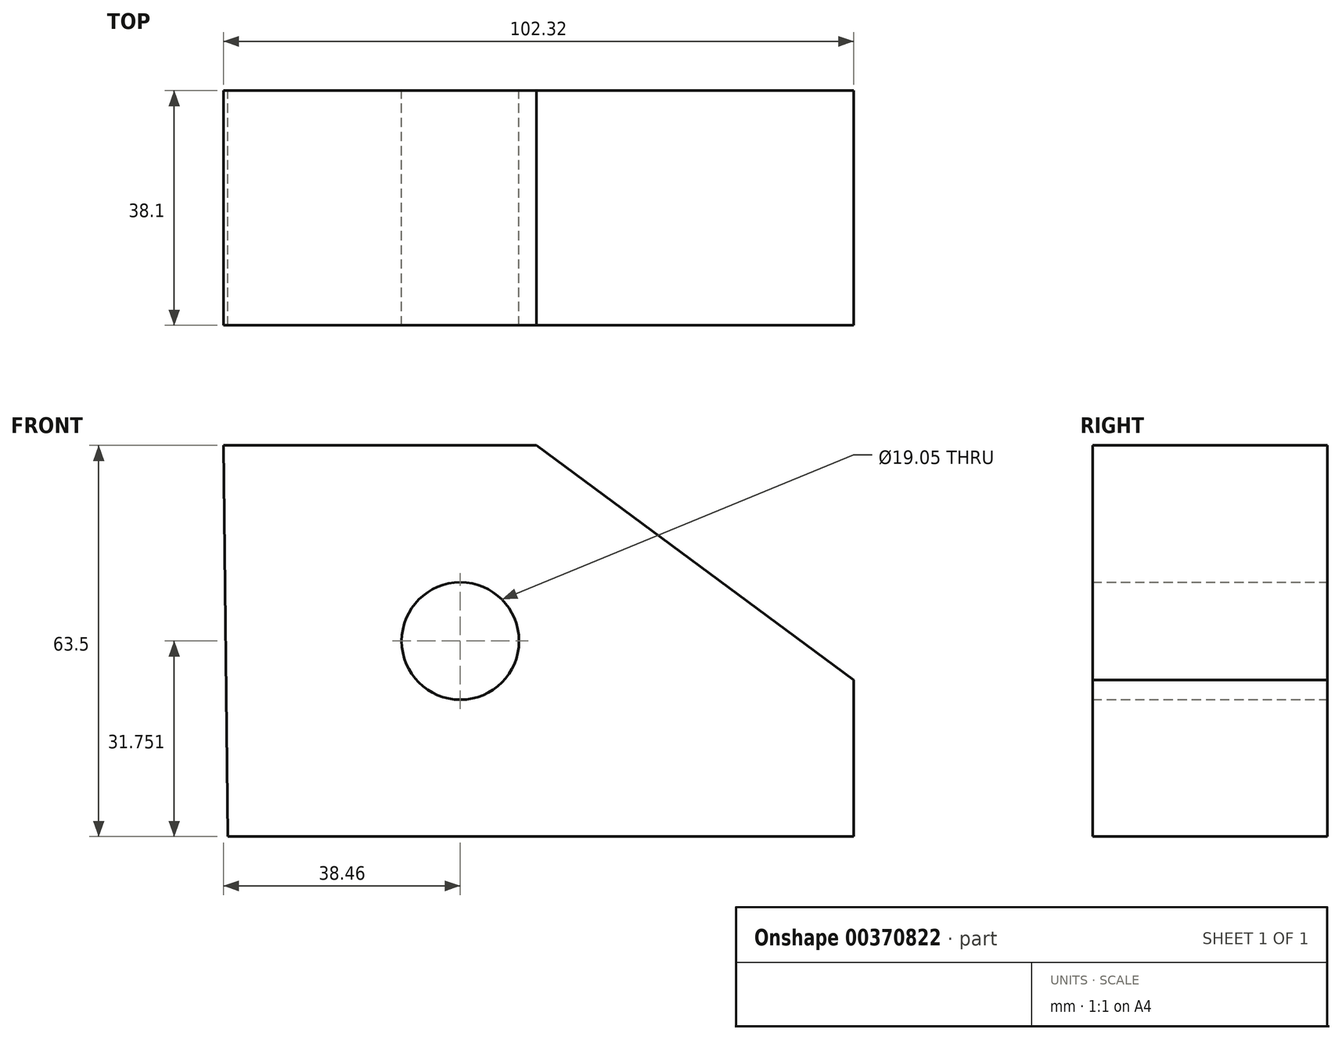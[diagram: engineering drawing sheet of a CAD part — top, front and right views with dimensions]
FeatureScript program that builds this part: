
annotation { "Feature Type Name" : "Feature", "Feature Type Description" : "" }
export const myFeature = defineFeature(function(context is Context, id is Id, definition is map)
    precondition{}
    {
        {
            var Q0;
            Q0=qCreatedBy(makeId("Front.planeOp"),FACE);
            var sketch = newSketch(context, id + "F0", { "sketchPlane" : qUnion([Q0])});
            skLineSegment(sketch, "E0", {"start": v(-38.46, -190.7) * mm, "end": v(12.34, -190.7) * mm});
            skLineSegment(sketch, "E1", {"start": v(12.34, -190.7) * mm, "end": v(63.86, -228.8) * mm});
            skLineSegment(sketch, "E2", {"start": v(63.86, -228.8) * mm, "end": v(63.86, -254.2) * mm});
            skLineSegment(sketch, "E3", {"start": v(63.86, -254.2) * mm, "end": v(-37.74, -254.2) * mm});
            skLineSegment(sketch, "E4", {"start": v(-37.74, -254.2) * mm, "end": v(-38.46, -190.7) * mm});
            skCircle(sketch, "E5", {"center": v(0, -222.45) * mm, "radius": 9.53 * mm});
            skSolve(sketch);
        }
        {
            var Q0;
            Q0=makeQuery(id+"F0.imprint","IMPRINT",FACE,{"disambiguationData":[TD([[makeQuery(id+"F0.imprint","IMPRINT",EDGE,{"derivedFrom":sQuery(id+"F0.wireOp",EDGE,"E0")}),-1.0]])]});
            extrude(context, id + "F1", {"entities" : qUnion([Q0]), "depth" : 38.1 * mm});
        }
    });
